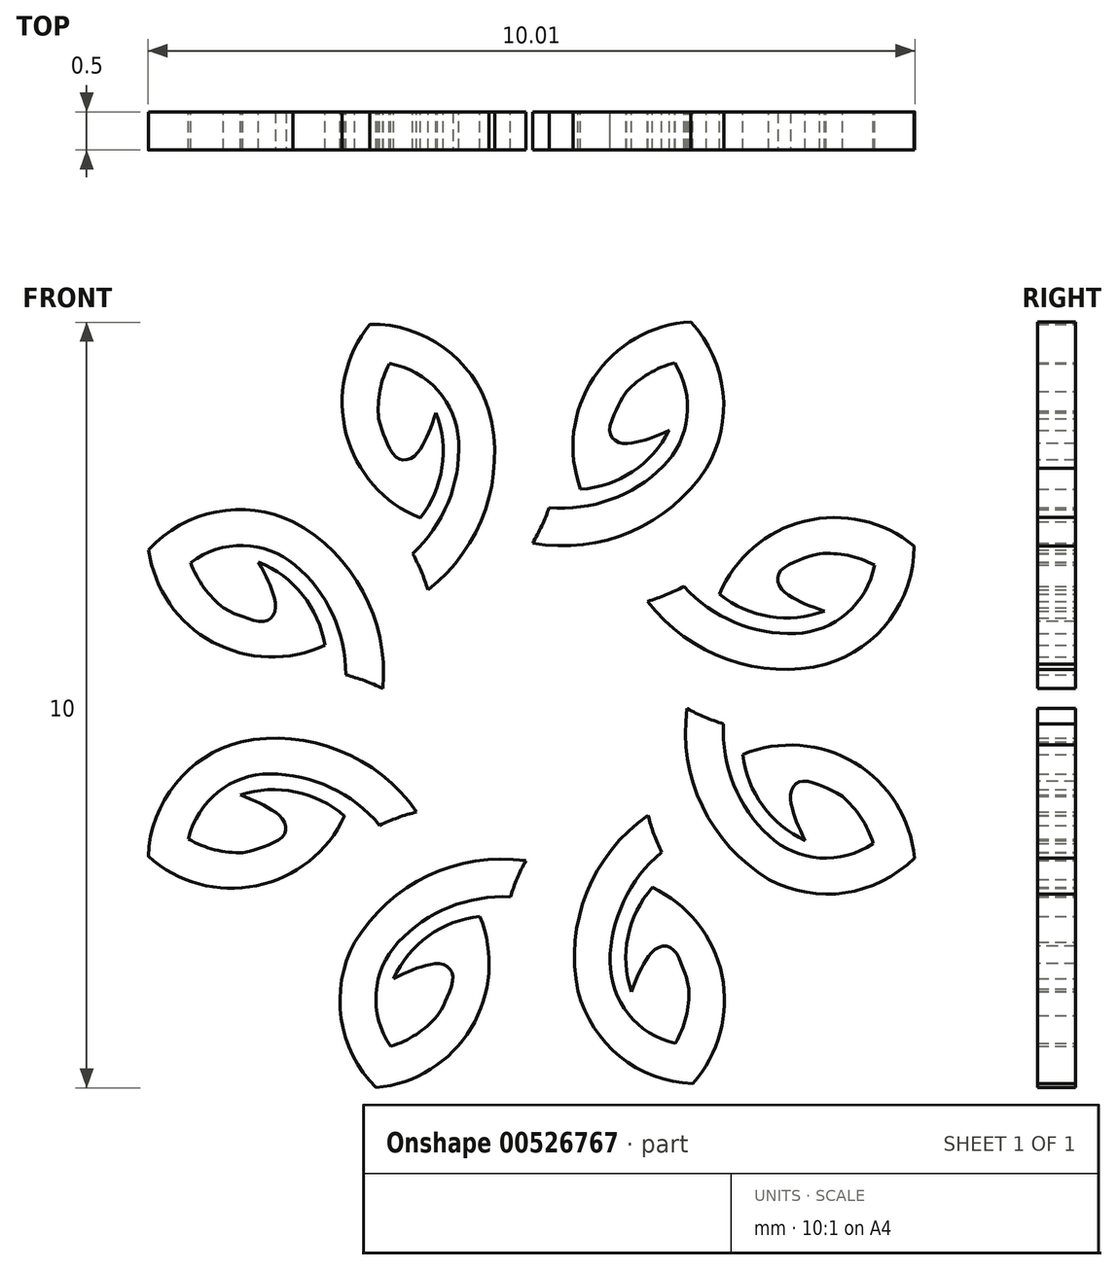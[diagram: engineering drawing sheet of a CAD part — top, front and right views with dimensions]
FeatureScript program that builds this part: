
annotation { "Feature Type Name" : "Feature", "Feature Type Description" : "" }
export const myFeature = defineFeature(function(context is Context, id is Id, definition is map)
    precondition{}
    {
        {
            var Q0;
            Q0=qCreatedBy(makeId("Front.planeOp"),FACE);
            var sketch = newSketch(context, id + "F0", { "sketchPlane" : qUnion([Q0])});
            skArc(sketch, "E0", {"start": v(-5.02, -2) * mm, "mid": v(-3.6, -2.39) * mm, "end": v(-2.45, -1.48) * mm});
            skArc(sketch, "E1", {"start": v(-3.8, -0.51) * mm, "mid": v(-4.66, -1.06) * mm, "end": v(-5.02, -2) * mm});
            skArc(sketch, "E2", {"start": v(-1.51, -1.43) * mm, "mid": v(-2.52, -0.62) * mm, "end": v(-3.8, -0.51) * mm});
            skArc(sketch, "E3", {"start": v(-1.51, -1.43) * mm, "mid": v(-1.76, -1.5) * mm, "end": v(-2, -1.6) * mm});
            skArc(sketch, "E4", {"start": v(-2, -1.6) * mm, "mid": v(-2.64, -1.1) * mm, "end": v(-3.43, -0.93) * mm});
            skArc(sketch, "E5", {"start": v(-3.43, -0.93) * mm, "mid": v(-4.1, -1.17) * mm, "end": v(-4.5, -1.78) * mm});
            skArc(sketch, "E6", {"start": v(-4.5, -1.78) * mm, "mid": v(-4.15, -1.92) * mm, "end": v(-3.78, -1.96) * mm});
            skArc(sketch, "E7", {"start": v(-2.45, -1.48) * mm, "mid": v(-3.1, -1.16) * mm, "end": v(-3.82, -1.2) * mm});
            skFitSpline(sketch, "E8", {"points": [v(-3.78, -1.96) * mm, v(-3.54, -1.9) * mm, v(-3.3, -1.78) * mm, v(-3.22, -1.66) * mm, v(-3.27, -1.51) * mm, v(-3.41, -1.4) * mm, v(-3.58, -1.3) * mm, v(-3.82, -1.2) * mm], "startDerivative": vector(2.41, 0.42) * mm, "endDerivative": vector(-1.55, 0.6) * mm});
            skArc(sketch, "E9", {"start": v(-2.04, -5.03) * mm, "mid": v(-0.8, -4.25) * mm, "end": v(-0.69, -2.8) * mm});
            skArc(sketch, "E10", {"start": v(-2.32, -3.13) * mm, "mid": v(-2.5, -4.12) * mm, "end": v(-2.04, -5.03) * mm});
            skArc(sketch, "E11", {"start": v(-0.09, -2.06) * mm, "mid": v(-1.36, -2.26) * mm, "end": v(-2.32, -3.13) * mm});
            skArc(sketch, "E12", {"start": v(-0.09, -2.06) * mm, "mid": v(-0.2, -2.3) * mm, "end": v(-0.29, -2.54) * mm});
            skArc(sketch, "E13", {"start": v(-0.29, -2.54) * mm, "mid": v(-1.09, -2.67) * mm, "end": v(-1.75, -3.13) * mm});
            skArc(sketch, "E14", {"start": v(-1.75, -3.13) * mm, "mid": v(-2.04, -3.8) * mm, "end": v(-1.85, -4.49) * mm});
            skArc(sketch, "E15", {"start": v(-1.85, -4.49) * mm, "mid": v(-1.52, -4.33) * mm, "end": v(-1.24, -4.09) * mm});
            skArc(sketch, "E16", {"start": v(-0.69, -2.8) * mm, "mid": v(-1.36, -3.05) * mm, "end": v(-1.82, -3.6) * mm});
            skFitSpline(sketch, "E17", {"points": [v(-1.24, -4.09) * mm, v(-1.12, -3.86) * mm, v(-1.04, -3.6) * mm, v(-1.08, -3.47) * mm, v(-1.22, -3.4) * mm, v(-1.4, -3.43) * mm, v(-1.59, -3.5) * mm, v(-1.82, -3.6) * mm], "startDerivative": vector(1.33, 2.06) * mm, "endDerivative": vector(-1.5, -0.73) * mm});
            skArc(sketch, "E18", {"start": v(-5.01, 2) * mm, "mid": v(-4.18, 0.8) * mm, "end": v(-2.71, 0.75) * mm});
            skArc(sketch, "E19", {"start": v(-3.13, 2.37) * mm, "mid": v(-4.13, 2.5) * mm, "end": v(-5.01, 2) * mm});
            skArc(sketch, "E20", {"start": v(-1.96, 0.19) * mm, "mid": v(-2.21, 1.45) * mm, "end": v(-3.13, 2.37) * mm});
            skArc(sketch, "E21", {"start": v(-1.96, 0.19) * mm, "mid": v(-2.2, 0.29) * mm, "end": v(-2.44, 0.36) * mm});
            skArc(sketch, "E22", {"start": v(-2.44, 0.36) * mm, "mid": v(-2.61, 1.15) * mm, "end": v(-3.1, 1.8) * mm});
            skArc(sketch, "E23", {"start": v(-3.1, 1.8) * mm, "mid": v(-3.78, 2.05) * mm, "end": v(-4.46, 1.83) * mm});
            skArc(sketch, "E24", {"start": v(-4.46, 1.83) * mm, "mid": v(-4.3, 1.5) * mm, "end": v(-4.03, 1.24) * mm});
            skArc(sketch, "E25", {"start": v(-2.71, 0.75) * mm, "mid": v(-3, 1.4) * mm, "end": v(-3.58, 1.84) * mm});
            skFitSpline(sketch, "E26", {"points": [v(-4.03, 1.24) * mm, v(-3.8, 1.13) * mm, v(-3.55, 1.06) * mm, v(-3.41, 1.1) * mm, v(-3.36, 1.25) * mm, v(-3.4, 1.43) * mm, v(-3.46, 1.61) * mm, v(-3.58, 1.84) * mm], "startDerivative": vector(2.12, -1.23) * mm, "endDerivative": vector(-0.8, 1.46) * mm});
            skArc(sketch, "E27", {"start": v(4.98, 2.05) * mm, "mid": v(3.55, 2.37) * mm, "end": v(2.44, 1.42) * mm});
            skArc(sketch, "E28", {"start": v(3.83, 0.5) * mm, "mid": v(4.66, 1.09) * mm, "end": v(4.98, 2.05) * mm});
            skArc(sketch, "E29", {"start": v(1.5, 1.33) * mm, "mid": v(2.54, 0.56) * mm, "end": v(3.83, 0.5) * mm});
            skArc(sketch, "E30", {"start": v(1.5, 1.33) * mm, "mid": v(1.74, 1.41) * mm, "end": v(1.98, 1.52) * mm});
            skArc(sketch, "E31", {"start": v(1.98, 1.52) * mm, "mid": v(2.64, 1.05) * mm, "end": v(3.43, 0.9) * mm});
            skArc(sketch, "E32", {"start": v(3.43, 0.9) * mm, "mid": v(4.1, 1.17) * mm, "end": v(4.46, 1.8) * mm});
            skArc(sketch, "E33", {"start": v(4.46, 1.8) * mm, "mid": v(4.12, 1.92) * mm, "end": v(3.75, 1.95) * mm});
            skArc(sketch, "E34", {"start": v(2.44, 1.42) * mm, "mid": v(3.1, 1.13) * mm, "end": v(3.81, 1.2) * mm});
            skFitSpline(sketch, "E35", {"points": [v(3.75, 1.95) * mm, v(3.5, 1.87) * mm, v(3.27, 1.75) * mm, v(3.2, 1.63) * mm, v(3.25, 1.49) * mm, v(3.4, 1.37) * mm, v(3.57, 1.29) * mm, v(3.81, 1.2) * mm], "startDerivative": vector(-2.4, -0.52) * mm, "endDerivative": vector(1.57, -0.54) * mm});
            skArc(sketch, "E36", {"start": v(2.07, 4.97) * mm, "mid": v(0.8, 4.24) * mm, "end": v(0.63, 2.79) * mm});
            skArc(sketch, "E37", {"start": v(2.27, 3.06) * mm, "mid": v(2.49, 4.05) * mm, "end": v(2.07, 4.97) * mm});
            skArc(sketch, "E38", {"start": v(0, 2.09) * mm, "mid": v(1.28, 2.23) * mm, "end": v(2.27, 3.06) * mm});
            skArc(sketch, "E39", {"start": v(0, 2.09) * mm, "mid": v(0.12, 2.31) * mm, "end": v(0.22, 2.55) * mm});
            skArc(sketch, "E40", {"start": v(0.22, 2.55) * mm, "mid": v(1.02, 2.65) * mm, "end": v(1.7, 3.09) * mm});
            skArc(sketch, "E41", {"start": v(1.7, 3.09) * mm, "mid": v(2.02, 3.74) * mm, "end": v(1.85, 4.44) * mm});
            skArc(sketch, "E42", {"start": v(1.85, 4.44) * mm, "mid": v(1.51, 4.3) * mm, "end": v(1.23, 4.07) * mm});
            skArc(sketch, "E43", {"start": v(0.63, 2.79) * mm, "mid": v(1.3, 3.02) * mm, "end": v(1.78, 3.56) * mm});
            skFitSpline(sketch, "E44", {"points": [v(1.23, 4.07) * mm, v(1.1, 3.84) * mm, v(1, 3.6) * mm, v(1.04, 3.46) * mm, v(1.18, 3.39) * mm, v(1.36, 3.4) * mm, v(1.55, 3.46) * mm, v(1.78, 3.56) * mm], "startDerivative": vector(-1.4, -2) * mm, "endDerivative": vector(1.52, 0.67) * mm});
            skArc(sketch, "E45", {"start": v(-2.12, 4.95) * mm, "mid": v(-2.43, 3.51) * mm, "end": v(-1.47, 2.41) * mm});
            skArc(sketch, "E46", {"start": v(-0.57, 3.82) * mm, "mid": v(-1.16, 4.64) * mm, "end": v(-2.12, 4.95) * mm});
            skArc(sketch, "E47", {"start": v(-1.37, 1.48) * mm, "mid": v(-0.62, 2.53) * mm, "end": v(-0.57, 3.82) * mm});
            skArc(sketch, "E48", {"start": v(-1.37, 1.48) * mm, "mid": v(-1.45, 1.72) * mm, "end": v(-1.57, 1.95) * mm});
            skArc(sketch, "E49", {"start": v(-1.57, 1.95) * mm, "mid": v(-1.1, 2.61) * mm, "end": v(-0.97, 3.41) * mm});
            skArc(sketch, "E50", {"start": v(-0.97, 3.41) * mm, "mid": v(-1.24, 4.08) * mm, "end": v(-1.87, 4.43) * mm});
            skArc(sketch, "E51", {"start": v(-1.87, 4.43) * mm, "mid": v(-2, 4.08) * mm, "end": v(-2.01, 3.71) * mm});
            skArc(sketch, "E52", {"start": v(-1.47, 2.41) * mm, "mid": v(-1.18, 3.07) * mm, "end": v(-1.26, 3.79) * mm});
            skFitSpline(sketch, "E53", {"points": [v(-2.01, 3.71) * mm, v(-1.93, 3.47) * mm, v(-1.8, 3.24) * mm, v(-1.69, 3.17) * mm, v(-1.54, 3.22) * mm, v(-1.43, 3.37) * mm, v(-1.35, 3.55) * mm, v(-1.26, 3.79) * mm], "startDerivative": vector(0.54, -2.39) * mm, "endDerivative": vector(0.52, 1.58) * mm});
            skArc(sketch, "E54", {"start": v(2.09, -4.97) * mm, "mid": v(2.47, -3.56) * mm, "end": v(1.56, -2.41) * mm});
            skArc(sketch, "E55", {"start": v(0.6, -3.77) * mm, "mid": v(1.14, -4.62) * mm, "end": v(2.09, -4.97) * mm});
            skArc(sketch, "E56", {"start": v(1.5, -1.47) * mm, "mid": v(0.7, -2.48) * mm, "end": v(0.6, -3.77) * mm});
            skArc(sketch, "E57", {"start": v(1.5, -1.47) * mm, "mid": v(1.58, -1.72) * mm, "end": v(1.68, -1.95) * mm});
            skArc(sketch, "E58", {"start": v(1.68, -1.95) * mm, "mid": v(1.19, -2.6) * mm, "end": v(1.01, -3.38) * mm});
            skArc(sketch, "E59", {"start": v(1.01, -3.38) * mm, "mid": v(1.25, -4.07) * mm, "end": v(1.86, -4.45) * mm});
            skArc(sketch, "E60", {"start": v(1.86, -4.45) * mm, "mid": v(2, -4.1) * mm, "end": v(2.04, -3.74) * mm});
            skArc(sketch, "E61", {"start": v(1.56, -2.41) * mm, "mid": v(1.25, -3.06) * mm, "end": v(1.29, -3.77) * mm});
            skFitSpline(sketch, "E62", {"points": [v(2.04, -3.74) * mm, v(1.97, -3.5) * mm, v(1.86, -3.25) * mm, v(1.74, -3.18) * mm, v(1.6, -3.22) * mm, v(1.48, -3.37) * mm, v(1.38, -3.54) * mm, v(1.29, -3.77) * mm], "startDerivative": vector(-0.42, 2.41) * mm, "endDerivative": vector(-0.6, -1.55) * mm});
            skArc(sketch, "E63", {"start": v(4.99, -2.03) * mm, "mid": v(4.2, -0.79) * mm, "end": v(2.75, -0.67) * mm});
            skArc(sketch, "E64", {"start": v(3.08, -2.3) * mm, "mid": v(4.08, -2.48) * mm, "end": v(4.99, -2.03) * mm});
            skArc(sketch, "E65", {"start": v(2.02, -0.08) * mm, "mid": v(2.22, -1.35) * mm, "end": v(3.08, -2.3) * mm});
            skArc(sketch, "E66", {"start": v(2.02, -0.08) * mm, "mid": v(2.25, -0.19) * mm, "end": v(2.5, -0.27) * mm});
            skArc(sketch, "E67", {"start": v(2.5, -0.27) * mm, "mid": v(2.63, -1.07) * mm, "end": v(3.09, -1.74) * mm});
            skArc(sketch, "E68", {"start": v(3.09, -1.74) * mm, "mid": v(3.75, -2.03) * mm, "end": v(4.45, -1.84) * mm});
            skArc(sketch, "E69", {"start": v(4.45, -1.84) * mm, "mid": v(4.29, -1.5) * mm, "end": v(4.04, -1.22) * mm});
            skArc(sketch, "E70", {"start": v(2.75, -0.67) * mm, "mid": v(3, -1.35) * mm, "end": v(3.56, -1.8) * mm});
            skFitSpline(sketch, "E71", {"points": [v(4.04, -1.22) * mm, v(3.82, -1.1) * mm, v(3.57, -1.02) * mm, v(3.43, -1.06) * mm, v(3.37, -1.2) * mm, v(3.4, -1.39) * mm, v(3.45, -1.57) * mm, v(3.56, -1.8) * mm], "startDerivative": vector(-2.06, 1.33) * mm, "endDerivative": vector(0.73, -1.5) * mm});
            skSolve(sketch);
        }
        {
            var Q0;
            Q0=makeQuery(id+"F0.imprint","IMPRINT",FACE,{"disambiguationData":[TD([[makeQuery(id+"F0.imprint","IMPRINT",EDGE,{"derivedFrom":sQuery(id+"F0.wireOp",EDGE,"E36")}),1.0]])]});
            var Q1;
            Q1=makeQuery(id+"F0.imprint","IMPRINT",FACE,{"disambiguationData":[TD([[makeQuery(id+"F0.imprint","IMPRINT",EDGE,{"derivedFrom":sQuery(id+"F0.wireOp",EDGE,"E54")}),1.0]])]});
            var Q2;
            Q2=makeQuery(id+"F0.imprint","IMPRINT",FACE,{"disambiguationData":[TD([[makeQuery(id+"F0.imprint","IMPRINT",EDGE,{"derivedFrom":sQuery(id+"F0.wireOp",EDGE,"E0")}),1.0]])]});
            var Q3;
            Q3=makeQuery(id+"F0.imprint","IMPRINT",FACE,{"disambiguationData":[TD([[makeQuery(id+"F0.imprint","IMPRINT",EDGE,{"derivedFrom":sQuery(id+"F0.wireOp",EDGE,"E45")}),1.0]])]});
            var Q4;
            Q4=makeQuery(id+"F0.imprint","IMPRINT",FACE,{"disambiguationData":[TD([[makeQuery(id+"F0.imprint","IMPRINT",EDGE,{"derivedFrom":sQuery(id+"F0.wireOp",EDGE,"E9")}),1.0]])]});
            var Q5;
            Q5=makeQuery(id+"F0.imprint","IMPRINT",FACE,{"disambiguationData":[TD([[makeQuery(id+"F0.imprint","IMPRINT",EDGE,{"derivedFrom":sQuery(id+"F0.wireOp",EDGE,"E27")}),1.0]])]});
            var Q6;
            Q6=makeQuery(id+"F0.imprint","IMPRINT",FACE,{"disambiguationData":[TD([[makeQuery(id+"F0.imprint","IMPRINT",EDGE,{"derivedFrom":sQuery(id+"F0.wireOp",EDGE,"E18")}),1.0]])]});
            var Q7;
            Q7=makeQuery(id+"F0.imprint","IMPRINT",FACE,{"disambiguationData":[TD([[makeQuery(id+"F0.imprint","IMPRINT",EDGE,{"derivedFrom":sQuery(id+"F0.wireOp",EDGE,"E63")}),1.0]])]});
            extrude(context, id + "F1", {"entities" : qUnion([Q0, Q1, Q2, Q3, Q4, Q5, Q6, Q7]), "depth" : 0.5 * mm, "offsetDistance" : 25 * mm});
        }
    });
